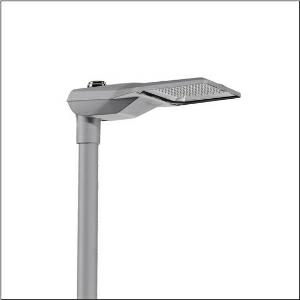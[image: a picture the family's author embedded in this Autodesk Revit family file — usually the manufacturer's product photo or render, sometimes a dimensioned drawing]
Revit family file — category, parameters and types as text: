
# Revit family: streetlight_sl_21_midi___st1_0a_5xe7d67n08mb_a1db
name_source: partatom
category: Lighting Fixtures
units: mm (PartAtom-declared; Revit-internal decimal feet)

## family parameters
Cut with Voids When Loaded = No
Host = Face
Light Source = No
Part Type = Normal
Room Calculation Point = No
Round Connector Dimension = Use Diameter
Shared = No

## types (1)
- --- (1 x LED, 16240 lm, 134.3 W, 2700K)
    Apparent Load = 134 VA
    CIE Flux Codes = 37 72 97 100 100
    Color Rendering = 70
    Color Temperature = 2700K
    Default Elevation = 1800 mm
    Description = Streetlight SL 21 midi, mast luminaire, primary light control with lens, of PMMA, primary optical cover: cover, of toughened safety glass, transparent, light distribution: ST1.0a, light emission: direct distribution, primary light characteristic: asymmetric, installation type: side-entry, LED, 3G 2.5mm², High Power LED, rated luminous flux: 16.240lm, luminous efficacy: 121lm/W, light colour: 727, colour temperature: 2700K, control gear: NEMA (7pin), control: overheat protection, pre-setting: linear dimming characteristic, constant luminous flux control, time-dependent luminous flux control, flexible luminous flux parameterisation, mains connection: 220..240V, AC, 50/60Hz, connection cable pre-assembled, cable length: 12,5m, wiring characteristics: H05VV-F, start of lifetime: 134W, end of service life: 141W, reduction: 60W, luminaire housing, of diecast aluminium (EN AC-44300), powder-coated, SITECO metallic grey (DB 702S), corrosivity category C5 high according to DIN EN ISO 12944, multi-level sealing system, sealing non-destructively replaceable, inclination adjustable: 0°, 5°, 10°, 15°, length: 644mm, width: 335mm, height: 110mm, spigot size: 42mm (side-entry), mounting height: 4..8m, protection rating (complete): IP66, insulation class (complete): insulation class I (protective earthing), certification: CE, ENEC, ENEC+, VDE, impact resistance: IK10, permissible operating ambient temperature for outdoor applications: -40..+50°C, standard-compliant lighting for roads and squares, packaging unit: 1 piece

Light Distribution: ST1.0a
    Height = 111 mm
    Lamp = 1 x LED
    Lamp Light Flux = 16240 lm
    Lamp Power = 134.3 W
    Lamp count = 1
    Length = 644 mm
    Luminous efficacy = 121 lm/W
    Manufacturer = Siteco
    ModVariant = No
    Model = 5XE7D67N08MB
    Number of Poles = 1
    OnlyDefault = Yes
    Power Factor = 1
    Product Name = Streetlight SL 21 midi | ST1.0a
    Product group = mast luminaire | pylon top
    ProductGroupID = 6100
    Protection Class = Protection class I
    Protection Degree = IP 66
    RLX_Detail_Level = 1
    RLX_Emergency_Light_Flux = 0 lm
    RLX_Emergency_Type = 0
    RLX_Emergency_Type_DB = No
    RlxData = <blob elided: 26469 chars, md5=f5c45c1f>
    Socket = socket
    Standby Power = 0 W
    System Light Flux = 16240 lm
    System Power = 134 W
    Type Comments = factory setting: luminous flux: 100 % | dim-lin: 254 | 687 mA
    Type Image = l_1294377.jpg
    URL = http://relux.com
    VarID = @adj_135389
    Voltage = 0 V
    Weight = 0.00 kg
    Width = 336 mm

## geometry (parser evidence)
native form markers: Blend x4, Sweep x13
no freeform markers — native parametric forms only
